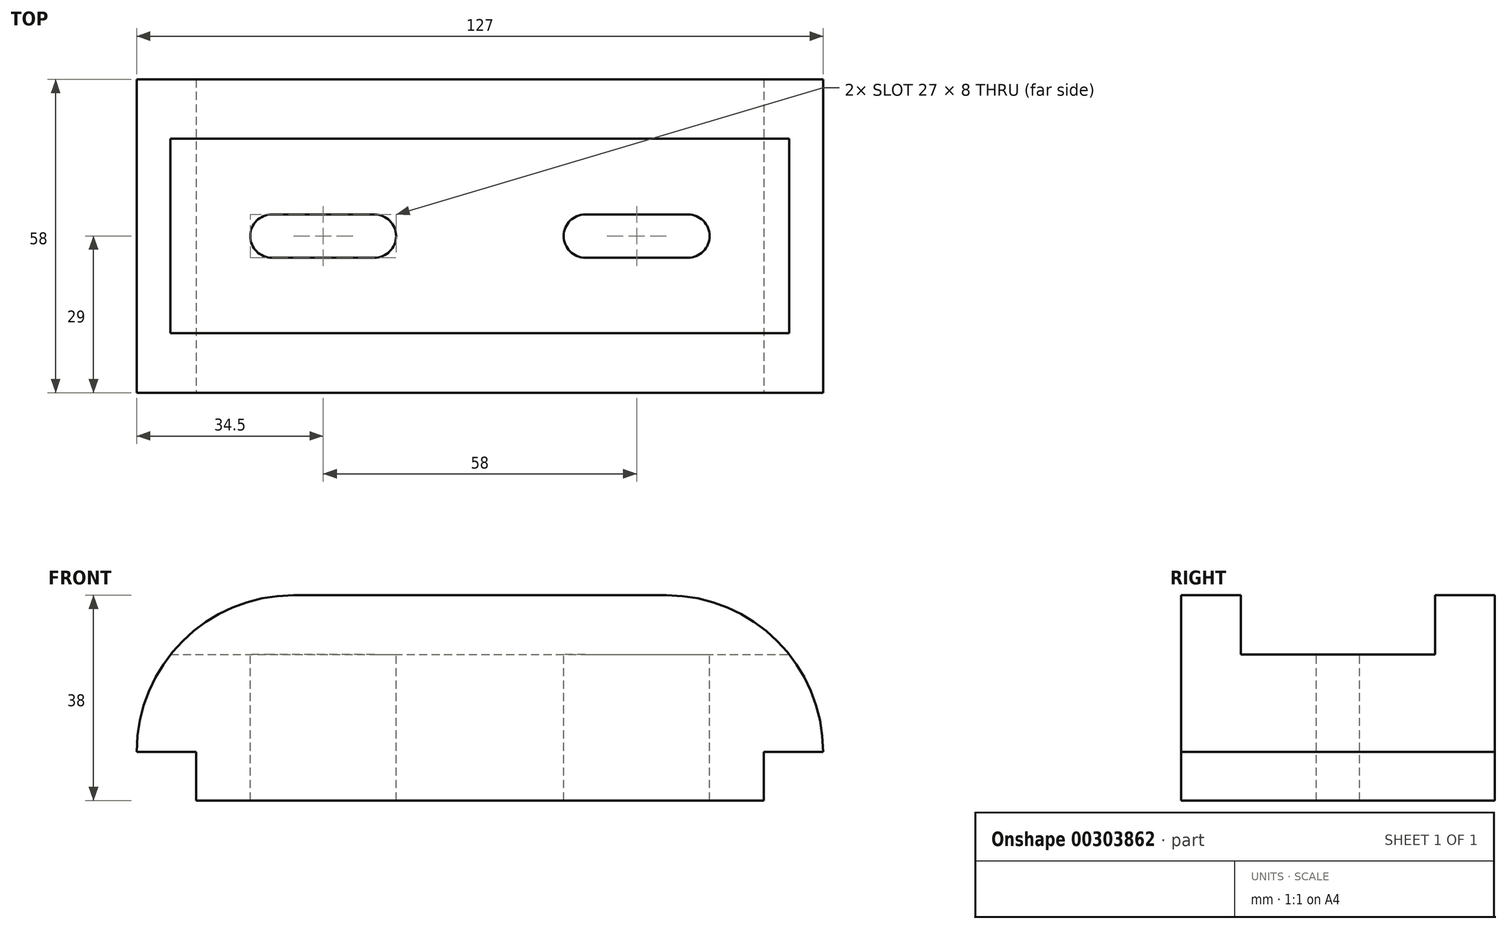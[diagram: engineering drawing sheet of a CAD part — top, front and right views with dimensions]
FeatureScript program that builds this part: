
annotation { "Feature Type Name" : "Feature", "Feature Type Description" : "" }
export const myFeature = defineFeature(function(context is Context, id is Id, definition is map)
    precondition{}
    {
        {
            var Q0;
            Q0=qCreatedBy(makeId("Front.planeOp"),FACE);
            var sketch = newSketch(context, id + "F0", { "sketchPlane" : qUnion([Q0])});
            skLineSegment(sketch, "E0", {"start": v(0, 0) * mm, "end": v(127, 0) * mm});
            skLineSegment(sketch, "E1", {"start": v(127, 0) * mm, "end": v(127, 9) * mm});
            skLineSegment(sketch, "E2", {"start": v(0, 0) * mm, "end": v(0, 9) * mm});
            skArc(sketch, "E3", {"start": v(29, 38) * mm, "mid": v(8.5, 29.5) * mm, "end": v(0, 9) * mm});
            skLineSegment(sketch, "E4", {"start": v(29, 38) * mm, "end": v(98, 38) * mm});
            skArc(sketch, "E5", {"start": v(127, 9) * mm, "mid": v(118.5, 29.5) * mm, "end": v(98, 38) * mm});
            skSolve(sketch);
        }
        {
            var Q0;
            Q0 = qSketchRegion(id + "F0", true);
            extrude(context, id + "F1", {"entities" : qUnion([Q0]), "oppositeDirection" : true, "depth" : 58 * mm});
        }
        {
            var Q0;
            Q0=makeQuery(id+"F1.opExtrude","SWEPT_FACE",FACE,{"disambiguationData":[OSD([sQuery(id+"F0.wireOp",EDGE,"E4")])]});
            var sketch = newSketch(context, id + "F2", { "sketchPlane" : qUnion([Q0])});
            skLineSegment(sketch, "E6", {"start": v(0, 0) * mm, "end": v(0, 11) * mm});
            skLineSegment(sketch, "E7", {"start": v(0, 11) * mm, "end": v(0, 47) * mm});
            skLineSegment(sketch, "E8", {"start": v(127, 47) * mm, "end": v(127, 11) * mm});
            skLineSegment(sketch, "E9", {"start": v(0, 47) * mm, "end": v(127, 47) * mm});
            skLineSegment(sketch, "E10", {"start": v(127, 11) * mm, "end": v(0, 11) * mm});
            skSolve(sketch);
        }
        {
            var Q0;
            Q0 = qSketchRegion(id + "F2", true);
            extrude(context, id + "F3", {"entities" : qUnion([Q0]), "operationType" : NewBodyOperationType.REMOVE, "oppositeDirection" : true, "depth" : 11 * mm});
        }
        {
            var Q0;
            Q0=makeQuery(id+"F1.opExtrude","CAP_FACE",FACE,{"disambiguationData":[OSD([sQuery(id+"F0.wireOp",EDGE,"E0"),sQuery(id+"F0.wireOp",EDGE,"E1"),sQuery(id+"F0.wireOp",EDGE,"E2"),sQuery(id+"F0.wireOp",EDGE,"E3"),sQuery(id+"F0.wireOp",EDGE,"E4"),sQuery(id+"F0.wireOp",EDGE,"E5")])],"isStart":true});
            var sketch = newSketch(context, id + "F4", { "sketchPlane" : qUnion([Q0])});
            skLineSegment(sketch, "E11", {"start": v(0, 0) * mm, "end": v(0, 9) * mm});
            skLineSegment(sketch, "E12", {"start": v(0, 9) * mm, "end": v(11, 9) * mm});
            skLineSegment(sketch, "E13", {"start": v(11, 9) * mm, "end": v(11, 0) * mm});
            skLineSegment(sketch, "E14", {"start": v(11, 0) * mm, "end": v(0, 0) * mm});
            skLineSegment(sketch, "E15", {"start": v(127, 0) * mm, "end": v(127, 9) * mm});
            skLineSegment(sketch, "E16", {"start": v(127, 9) * mm, "end": v(116, 9) * mm});
            skLineSegment(sketch, "E17", {"start": v(116, 9) * mm, "end": v(116, 0) * mm});
            skLineSegment(sketch, "E18", {"start": v(116, 0) * mm, "end": v(127, 0) * mm});
            skSolve(sketch);
        }
        {
            var Q0;
            Q0=makeQuery(id+"F4.imprint","IMPRINT",FACE,{"disambiguationData":[TD([[makeQuery(id+"F4.imprint","IMPRINT",EDGE,{"derivedFrom":sQuery(id+"F4.wireOp",EDGE,"E11")}),-1.0]])]});
            var Q1;
            Q1=makeQuery(id+"F4.imprint","IMPRINT",FACE,{"disambiguationData":[TD([[makeQuery(id+"F4.imprint","IMPRINT",EDGE,{"derivedFrom":sQuery(id+"F4.wireOp",EDGE,"E15")}),1.0]])]});
            extrude(context, id + "F5", {"entities" : qUnion([Q0, Q1]), "operationType" : NewBodyOperationType.REMOVE, "oppositeDirection" : true, "depth" : 58 * mm});
        }
        {
            var Q0;
            {var subQ0=sQuery(id+"F2.wireOp",EDGE,"E9");var subQ1=sQuery(id+"F0.wireOp",EDGE,"E4");var subQ2=makeQuery(id+"F1.opExtrude","SWEPT_EDGE",EDGE,{"disambiguationData":[OSD([sQuery(id+"F0.wireOp",EDGE,"E3"),subQ1])]});var subQ3=makeQuery(id+"F2.imprint","INTERSECT",VERTEX,{"derivedFrom":[subQ2,subQ0]});Q0=makeQuery(id+"F2.imprint","IMPRINT",FACE,{"disambiguationData":[TD([[makeQuery(id+"F2.imprint","IMPRINT",EDGE,{"disambiguationData":[TD([[subQ3,-1.0]])],"derivedFrom":subQ0}),-1.0]])]});}
            var sketch = newSketch(context, id + "F6", { "sketchPlane" : qUnion([Q0])});
            skArc(sketch, "E19", {"start": v(25, 33) * mm, "mid": v(21, 29) * mm, "end": v(25, 25) * mm});
            skArc(sketch, "E20", {"start": v(44, 33) * mm, "mid": v(48, 29) * mm, "end": v(44, 25) * mm});
            skLineSegment(sketch, "E21", {"start": v(25, 33) * mm, "end": v(44, 33) * mm});
            skLineSegment(sketch, "E22", {"start": v(44, 25) * mm, "end": v(25, 25) * mm});
            skArc(sketch, "E23", {"start": v(83, 33) * mm, "mid": v(79, 29) * mm, "end": v(83, 25) * mm});
            skArc(sketch, "E24", {"start": v(102, 33) * mm, "mid": v(106, 29) * mm, "end": v(102, 25) * mm});
            skLineSegment(sketch, "E25", {"start": v(83, 33) * mm, "end": v(102, 33) * mm});
            skLineSegment(sketch, "E26", {"start": v(102, 25) * mm, "end": v(83, 25) * mm});
            skSolve(sketch);
        }
        {
            var Q0;
            Q0 = qSketchRegion(id + "F6", true);
            extrude(context, id + "F7", {"entities" : qUnion([Q0]), "operationType" : NewBodyOperationType.REMOVE, "oppositeDirection" : true, "depth" : 58 * mm});
        }
    });
